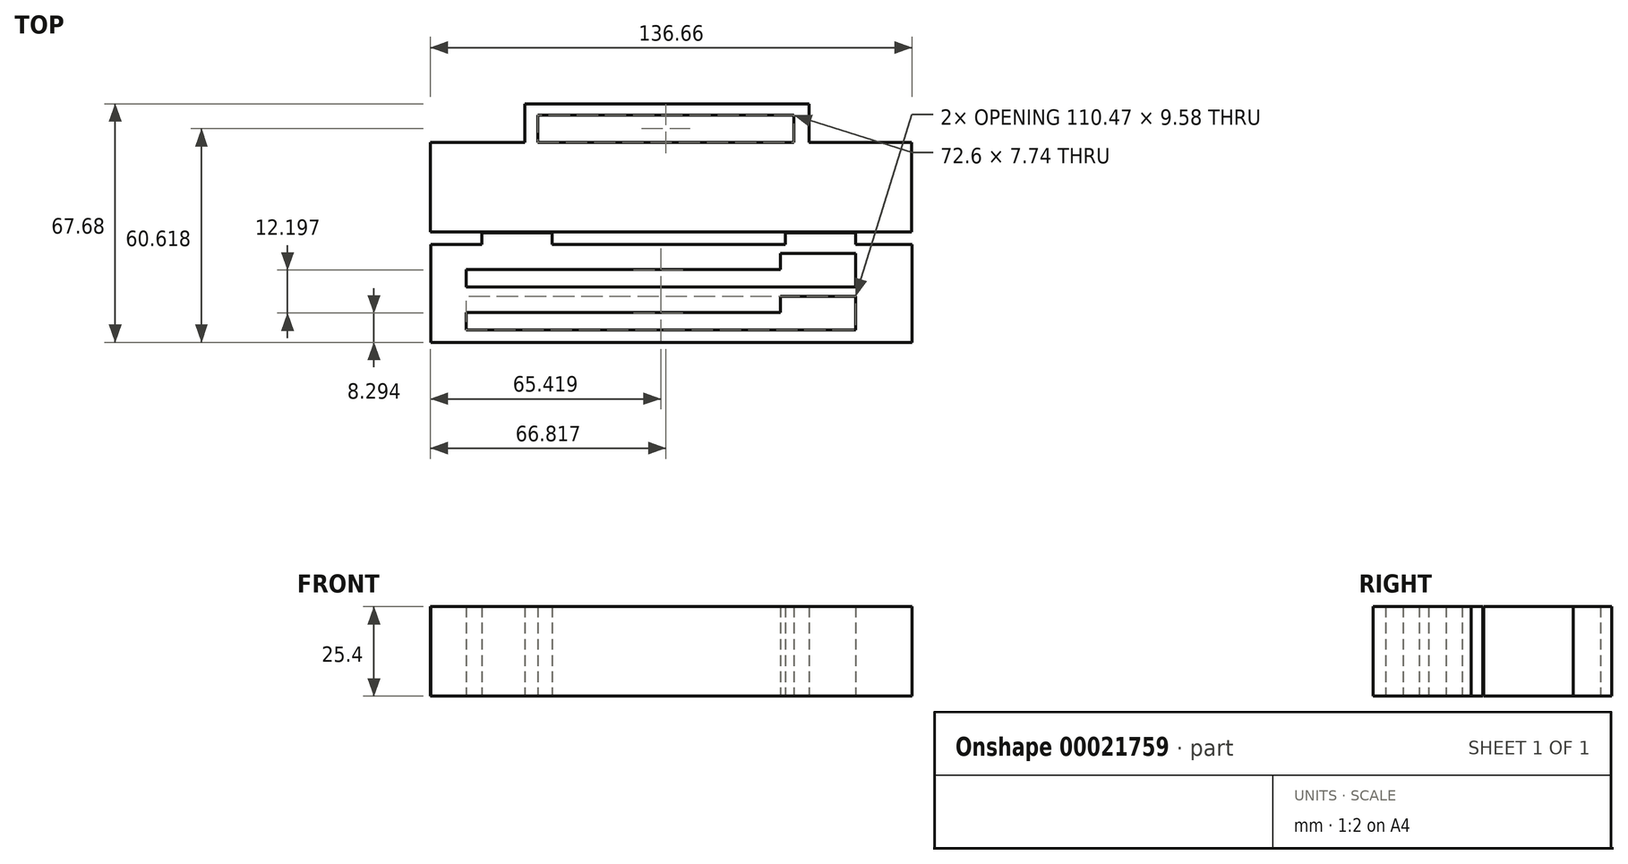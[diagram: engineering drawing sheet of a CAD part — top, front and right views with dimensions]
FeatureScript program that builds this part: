
annotation { "Feature Type Name" : "Feature", "Feature Type Description" : "" }
export const myFeature = defineFeature(function(context is Context, id is Id, definition is map)
    precondition{}
    {
        {
            var Q0;
            Q0=qCreatedBy(makeId("Top.planeOp"),FACE);
            var sketch = newSketch(context, id + "F0", { "sketchPlane" : qUnion([Q0])});
            skLineSegment(sketch, "E0.bottom", {"start": v(-68.37, -26.12) * mm, "end": v(68.1, -26.12) * mm});
            skLineSegment(sketch, "E0.top", {"start": v(-68.37, -53.9) * mm, "end": v(68.1, -53.9) * mm});
            skLineSegment(sketch, "E0.left", {"start": v(-68.37, -26.12) * mm, "end": v(-68.37, -53.9) * mm});
            skLineSegment(sketch, "E0.right", {"start": v(68.1, -26.12) * mm, "end": v(68.1, -53.9) * mm});
            skLineSegment(sketch, "E1.bottom", {"start": v(-53.95, -26.12) * mm, "end": v(-33.95, -26.12) * mm});
            skLineSegment(sketch, "E1.top", {"start": v(-53.95, -22.86) * mm, "end": v(-33.95, -22.86) * mm});
            skLineSegment(sketch, "E1.left", {"start": v(-53.95, -26.12) * mm, "end": v(-53.95, -22.86) * mm});
            skLineSegment(sketch, "E1.right", {"start": v(-33.95, -26.12) * mm, "end": v(-33.95, -22.86) * mm});
            skLineSegment(sketch, "E2.bottom", {"start": v(52.1, -26.12) * mm, "end": v(32.09, -26.12) * mm});
            skLineSegment(sketch, "E2.top", {"start": v(52.1, -22.86) * mm, "end": v(32.09, -22.86) * mm});
            skLineSegment(sketch, "E2.left", {"start": v(52.1, -26.12) * mm, "end": v(52.1, -22.86) * mm});
            skLineSegment(sketch, "E2.right", {"start": v(32.09, -26.12) * mm, "end": v(32.09, -22.86) * mm});
            skLineSegment(sketch, "E3.bottom", {"start": v(-68.56, 2.86) * mm, "end": v(67.97, 2.86) * mm});
            skLineSegment(sketch, "E3.top", {"start": v(-68.56, -22.54) * mm, "end": v(67.97, -22.54) * mm});
            skLineSegment(sketch, "E3.left", {"start": v(-68.56, 2.86) * mm, "end": v(-68.56, -22.54) * mm});
            skLineSegment(sketch, "E3.right", {"start": v(67.97, 2.86) * mm, "end": v(67.97, -22.54) * mm});
            skLineSegment(sketch, "E4.bottom", {"start": v(-58.37, -33.25) * mm, "end": v(30.78, -33.25) * mm});
            skLineSegment(sketch, "E4.top", {"start": v(-58.37, -38.19) * mm, "end": v(30.78, -38.19) * mm});
            skLineSegment(sketch, "E4.left", {"start": v(-58.37, -33.25) * mm, "end": v(-58.37, -38.19) * mm});
            skLineSegment(sketch, "E5.bottom", {"start": v(30.78, -38.19) * mm, "end": v(52.1, -38.19) * mm});
            skLineSegment(sketch, "E5.top", {"start": v(30.78, -28.6) * mm, "end": v(52.1, -28.6) * mm});
            skLineSegment(sketch, "E5.right", {"start": v(52.1, -38.19) * mm, "end": v(52.1, -28.6) * mm});
            skLineSegment(sketch, "E6", {"start": v(30.78, -33.4) * mm, "end": v(30.78, -28.6) * mm});
            skLineSegment(sketch, "E7.bottom", {"start": v(-58.37, -45.45) * mm, "end": v(30.78, -45.45) * mm});
            skLineSegment(sketch, "E7.top", {"start": v(-58.37, -50.39) * mm, "end": v(30.78, -50.39) * mm});
            skLineSegment(sketch, "E7.left", {"start": v(-58.37, -45.45) * mm, "end": v(-58.37, -50.39) * mm});
            skLineSegment(sketch, "E8.bottom", {"start": v(30.78, -50.39) * mm, "end": v(52.1, -50.39) * mm});
            skLineSegment(sketch, "E8.top", {"start": v(30.78, -40.8) * mm, "end": v(52.1, -40.8) * mm});
            skLineSegment(sketch, "E8.right", {"start": v(52.1, -50.39) * mm, "end": v(52.1, -40.8) * mm});
            skLineSegment(sketch, "E9", {"start": v(30.78, -45.6) * mm, "end": v(30.78, -40.8) * mm});
            skLineSegment(sketch, "E10.bottom", {"start": v(-38.04, 2.86) * mm, "end": v(34.56, 2.86) * mm});
            skLineSegment(sketch, "E10.top", {"start": v(-38.04, 10.6) * mm, "end": v(34.56, 10.6) * mm});
            skLineSegment(sketch, "E10.left", {"start": v(-38.04, 2.86) * mm, "end": v(-38.04, 10.6) * mm});
            skLineSegment(sketch, "E10.right", {"start": v(34.56, 2.86) * mm, "end": v(34.56, 10.6) * mm});
            skLineSegment(sketch, "E11.bottom", {"start": v(-41.82, 2.86) * mm, "end": v(38.92, 2.86) * mm});
            skLineSegment(sketch, "E11.top", {"start": v(-41.82, 13.8) * mm, "end": v(38.92, 13.8) * mm});
            skLineSegment(sketch, "E11.left", {"start": v(-41.82, 2.86) * mm, "end": v(-41.82, 13.8) * mm});
            skLineSegment(sketch, "E11.right", {"start": v(38.92, 2.86) * mm, "end": v(38.92, 13.8) * mm});
            skPoint(sketch, "E12", {"position": v(25.27, 2.86) * mm});
            skLineSegment(sketch, "E13.top", {"start": v(24.14, 2.86) * mm, "end": v(28.46, 2.86) * mm});
            skSolve(sketch);
        }
        {
            var Q0;
            Q0 = qSketchRegion(id + "F0", true);
            extrude(context, id + "F1", {"entities" : qUnion([Q0]), "endBound" : BoundingType.SYMMETRIC, "depth" : 25.4 * mm});
        }
    });
